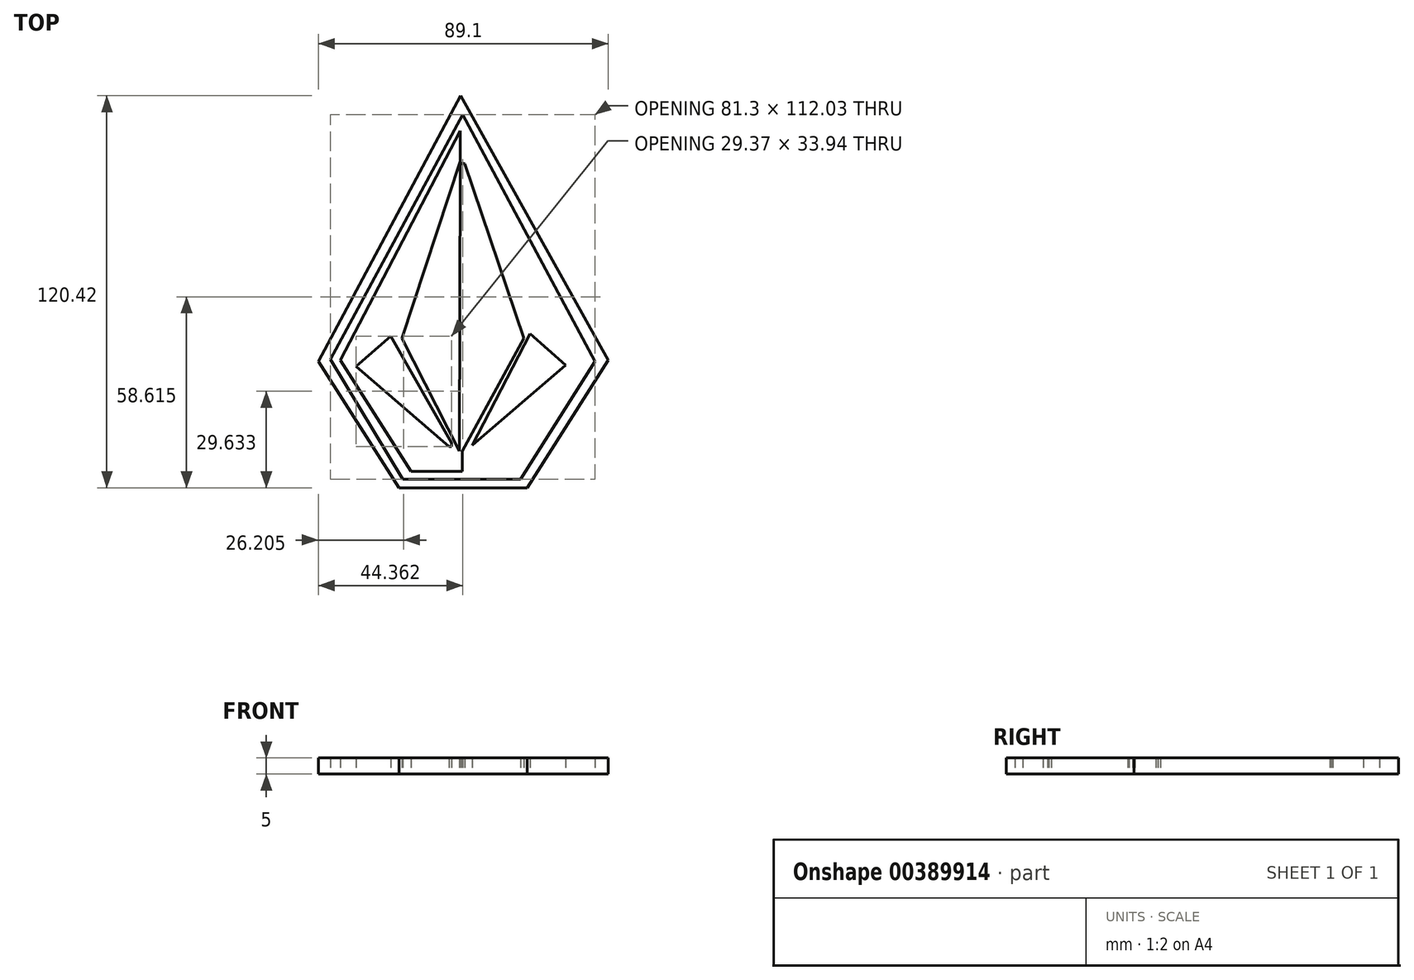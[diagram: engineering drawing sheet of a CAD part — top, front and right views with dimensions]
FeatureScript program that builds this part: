
annotation { "Feature Type Name" : "Feature", "Feature Type Description" : "" }
export const myFeature = defineFeature(function(context is Context, id is Id, definition is map)
    precondition{}
    {
        {
            var Q0;
            Q0=qCreatedBy(makeId("Top.planeOp"),FACE);
            var sketch = newSketch(context, id + "F0", { "sketchPlane" : qUnion([Q0])});
            skLineSegment(sketch, "E0", {"start": v(-42.79, -17.01) * mm, "end": v(0.88, 64.58) * mm});
            skLineSegment(sketch, "E1", {"start": v(0.88, 64.58) * mm, "end": v(46.3, -16.7) * mm});
            skLineSegment(sketch, "E2", {"start": v(46.3, -16.7) * mm, "end": v(21.42, -55.84) * mm});
            skLineSegment(sketch, "E3", {"start": v(21.42, -55.84) * mm, "end": v(-18.05, -55.84) * mm});
            skLineSegment(sketch, "E4", {"start": v(-18.05, -55.84) * mm, "end": v(-42.79, -17.01) * mm});
            skLineSegment(sketch, "E5", {"start": v(-39.08, -16.46) * mm, "end": v(-16.8, -53.24) * mm});
            skLineSegment(sketch, "E6", {"start": v(-16.8, -53.24) * mm, "end": v(19.4, -53.24) * mm});
            skLineSegment(sketch, "E7", {"start": v(19.4, -53.24) * mm, "end": v(42.22, -17.06) * mm});
            skLineSegment(sketch, "E8", {"start": v(42.22, -17.06) * mm, "end": v(1.62, 58.8) * mm});
            skLineSegment(sketch, "E9", {"start": v(1.62, 58.8) * mm, "end": v(-39.08, -16.46) * mm});
            skLineSegment(sketch, "E10", {"start": v(1, -50.85) * mm, "end": v(-14.27, -50.85) * mm});
            skLineSegment(sketch, "E11", {"start": v(-14.27, -50.85) * mm, "end": v(-36.07, -16.63) * mm});
            skLineSegment(sketch, "E12", {"start": v(-36.07, -16.63) * mm, "end": v(0.78, 53.85) * mm});
            skLineSegment(sketch, "E13", {"start": v(0.78, 53.85) * mm, "end": v(0.78, 44.47) * mm});
            skLineSegment(sketch, "E14", {"start": v(0.78, 44.47) * mm, "end": v(-17.08, -9.98) * mm});
            skLineSegment(sketch, "E15", {"start": v(-17.08, -9.98) * mm, "end": v(0.55, -44.57) * mm});
            skLineSegment(sketch, "E16", {"start": v(0.55, -44.57) * mm, "end": v(0.78, 43.53) * mm});
            skLineSegment(sketch, "E17", {"start": v(0.78, 43.53) * mm, "end": v(1.42, 43.94) * mm});
            skLineSegment(sketch, "E18", {"start": v(1.42, 43.94) * mm, "end": v(2.21, 43.68) * mm});
            skLineSegment(sketch, "E19", {"start": v(2.21, 43.68) * mm, "end": v(20.43, -9.98) * mm});
            skLineSegment(sketch, "E20", {"start": v(20.43, -9.98) * mm, "end": v(1.42, -44.57) * mm});
            skLineSegment(sketch, "E21", {"start": v(1.42, -44.57) * mm, "end": v(1.42, -50.85) * mm});
            skLineSegment(sketch, "E22", {"start": v(1.42, -50.85) * mm, "end": v(1, -50.85) * mm});
            skLineSegment(sketch, "E23", {"start": v(22.27, -8.58) * mm, "end": v(33.17, -18.15) * mm});
            skLineSegment(sketch, "E24", {"start": v(33.17, -18.15) * mm, "end": v(4.44, -42.76) * mm});
            skLineSegment(sketch, "E25", {"start": v(-31.27, -18.54) * mm, "end": v(-20.58, -9.24) * mm});
            skLineSegment(sketch, "E26", {"start": v(-20.58, -9.24) * mm, "end": v(-1.9, -42.04) * mm});
            skLineSegment(sketch, "E27", {"start": v(-1.9, -42.04) * mm, "end": v(-1.9, -43.18) * mm});
            skLineSegment(sketch, "E28", {"start": v(-1.9, -43.18) * mm, "end": v(-2.61, -43.18) * mm});
            skLineSegment(sketch, "E29", {"start": v(-2.61, -43.18) * mm, "end": v(-31.27, -18.54) * mm});
            skLineSegment(sketch, "E30", {"start": v(4.44, -42.76) * mm, "end": v(22.27, -8.58) * mm});
            skSolve(sketch);
        }
        {
            var Q0;
            Q0=makeQuery(id+"F0.imprint","IMPRINT",FACE,{"disambiguationData":[TD([[makeQuery(id+"F0.imprint","IMPRINT",EDGE,{"derivedFrom":sQuery(id+"F0.wireOp",EDGE,"E0")}),-1.0]])]});
            var Q1;
            Q1=makeQuery(id+"F0.imprint","IMPRINT",FACE,{"disambiguationData":[TD([[makeQuery(id+"F0.imprint","IMPRINT",EDGE,{"derivedFrom":sQuery(id+"F0.wireOp",EDGE,"E10")}),-1.0]])]});
            var Q2;
            Q2=makeQuery(id+"F0.imprint","IMPRINT",FACE,{"disambiguationData":[TD([[makeQuery(id+"F0.imprint","IMPRINT",EDGE,{"derivedFrom":sQuery(id+"F0.wireOp",EDGE,"E23")}),-1.0]])]});
            extrude(context, id + "F1", {"entities" : qUnion([Q0, Q1, Q2]), "depth" : 5 * mm});
        }
    });
